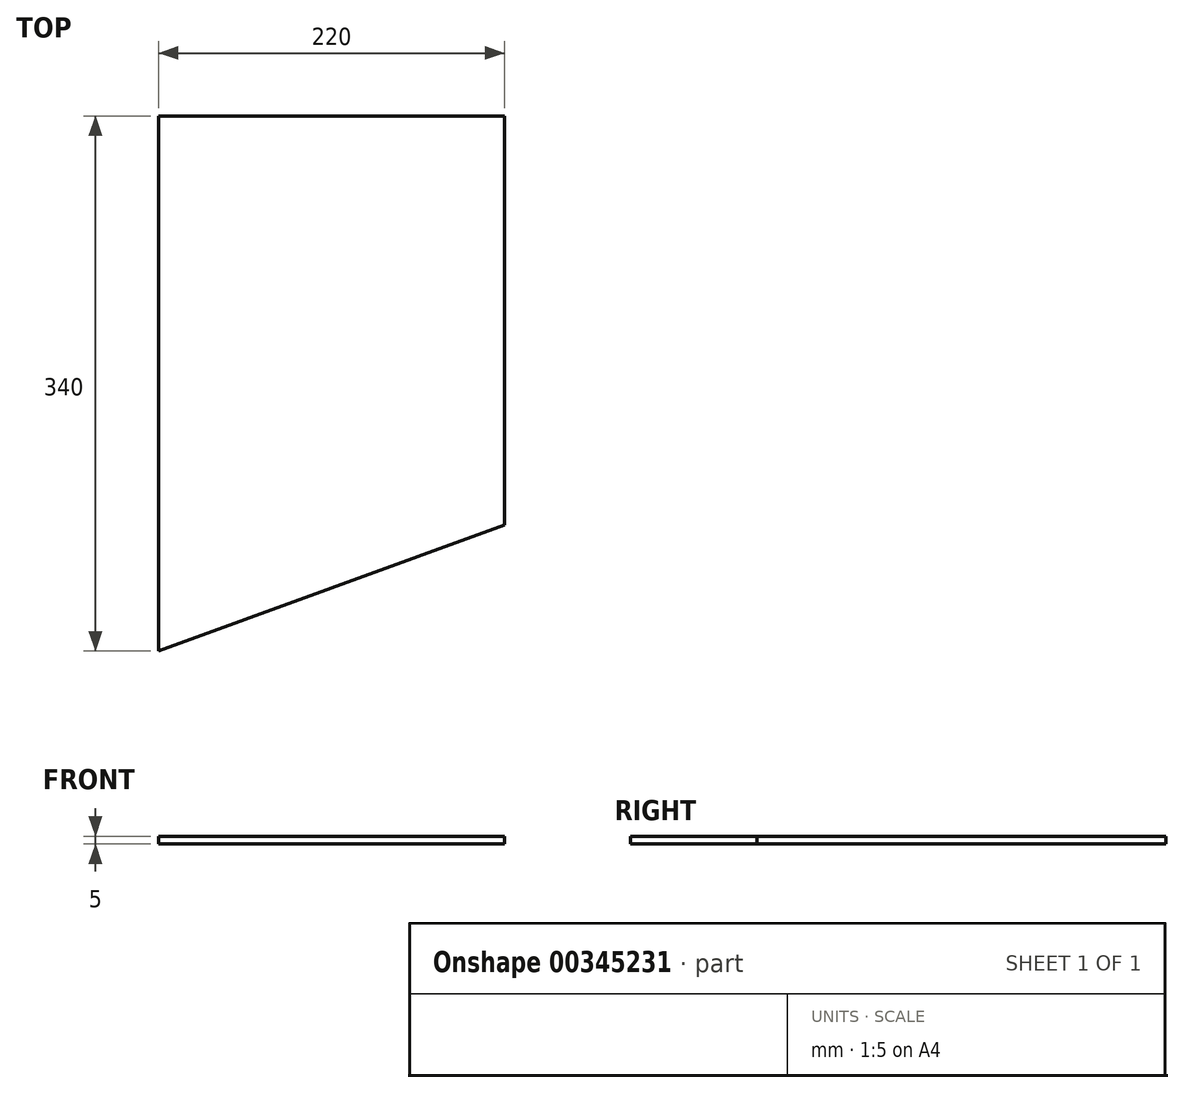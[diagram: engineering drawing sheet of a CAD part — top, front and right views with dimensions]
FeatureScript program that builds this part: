
annotation { "Feature Type Name" : "Feature", "Feature Type Description" : "" }
export const myFeature = defineFeature(function(context is Context, id is Id, definition is map)
    precondition{}
    {
        {
            var Q0;
            Q0=qCreatedBy(makeId("Top.planeOp"),FACE);
            var sketch = newSketch(context, id + "F0", { "sketchPlane" : qUnion([Q0])});
            skPoint(sketch, "E0.middle", {"position": v(0, 0) * mm});
            skLineSegment(sketch, "E1.bottom", {"start": v(-110, 170) * mm, "end": v(110, 170) * mm});
            skLineSegment(sketch, "E1.left", {"start": v(-110, 170) * mm, "end": v(-110, -170) * mm});
            skLineSegment(sketch, "E1.right", {"start": v(110, 170) * mm, "end": v(110, -89.93) * mm});
            skLineSegment(sketch, "E2", {"start": v(-110, -170) * mm, "end": v(110, -89.93) * mm});
            skSolve(sketch);
        }
        {
            var Q0;
            Q0=qSketchRegion(id+"F0",true);
            extrude(context, id + "F1", {"entities" : qUnion([Q0]), "depth" : 5 * mm});
        }
    });
